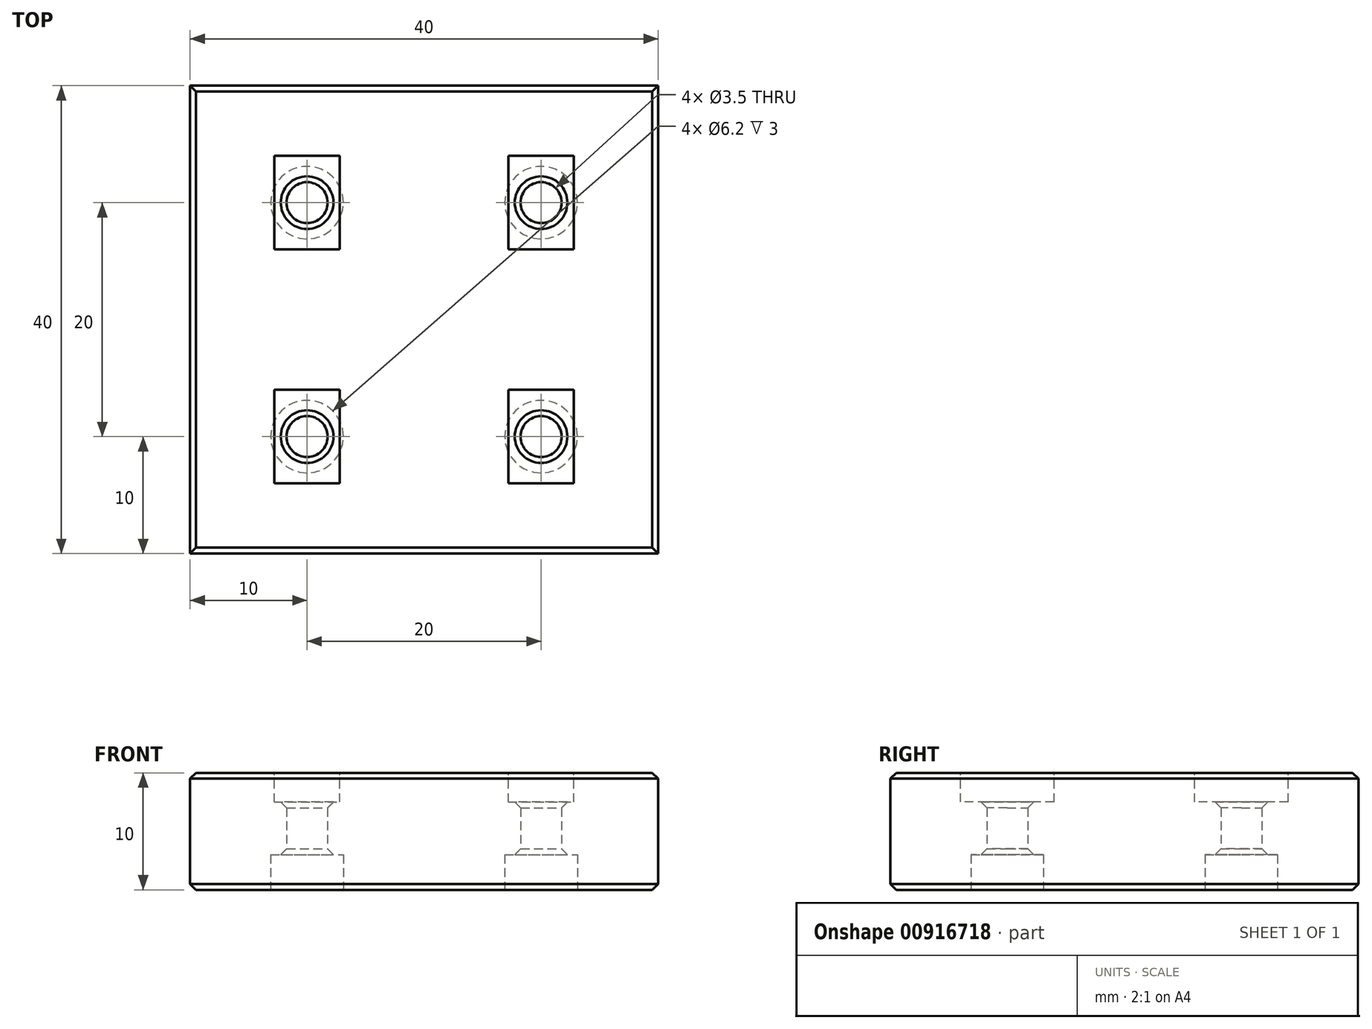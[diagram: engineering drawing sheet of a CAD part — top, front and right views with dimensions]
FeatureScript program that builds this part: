
annotation { "Feature Type Name" : "Feature", "Feature Type Description" : "" }
export const myFeature = defineFeature(function(context is Context, id is Id, definition is map)
    precondition{}
    {
        {
            var Q0;
            Q0=qCreatedBy(makeId("Top.planeOp"),FACE);
            var sketch = newSketch(context, id + "F0", { "sketchPlane" : qUnion([Q0])});
            skLineSegment(sketch, "E0.bottom", {"start": v(-20, 20) * mm, "end": v(20, 20) * mm});
            skLineSegment(sketch, "E0.top", {"start": v(-20, -20) * mm, "end": v(20, -20) * mm});
            skLineSegment(sketch, "E0.left", {"start": v(-20, 20) * mm, "end": v(-20, -20) * mm});
            skLineSegment(sketch, "E0.right", {"start": v(20, 20) * mm, "end": v(20, -20) * mm});
            skCircle(sketch, "E1", {"center": v(-10, 10) * mm, "radius": 1.75 * mm});
            skCircle(sketch, "E2", {"center": v(10, 10) * mm, "radius": 1.75 * mm});
            skCircle(sketch, "E3", {"center": v(10, -10) * mm, "radius": 1.75 * mm});
            skCircle(sketch, "E4", {"center": v(-10, -10) * mm, "radius": 1.75 * mm});
            skSolve(sketch);
        }
        {
            var Q0;
            Q0 = qSketchRegion(id + "F0", true);
            extrude(context, id + "F1", {"entities" : qUnion([Q0]), "depth" : 10 * mm, "offsetDistance" : 25 * mm});
        }
        {
            var Q0;
            Q0=makeQuery(id+"F1.opExtrude","CAP_FACE",FACE,{"disambiguationData":[OSD([sQuery(id+"F0.wireOp",EDGE,"E0.bottom"),sQuery(id+"F0.wireOp",EDGE,"E0.top"),sQuery(id+"F0.wireOp",EDGE,"E0.left"),sQuery(id+"F0.wireOp",EDGE,"E0.right"),sQuery(id+"F0.wireOp",EDGE,"E1"),sQuery(id+"F0.wireOp",EDGE,"E2"),sQuery(id+"F0.wireOp",EDGE,"E3"),sQuery(id+"F0.wireOp",EDGE,"E4")])],"isStart":true});
            var sketch = newSketch(context, id + "F2", { "sketchPlane" : qUnion([Q0])});
            skCircle(sketch, "E5", {"center": v(10, 10) * mm, "radius": 3.1 * mm});
            skCircle(sketch, "E6", {"center": v(10, -10) * mm, "radius": 3.1 * mm});
            skCircle(sketch, "E7", {"center": v(-10, -10) * mm, "radius": 3.1 * mm});
            skCircle(sketch, "E8", {"center": v(-10, 10) * mm, "radius": 3.1 * mm});
            skSolve(sketch);
        }
        {
            var Q0;
            Q0 = qSketchRegion(id + "F2", true);
            extrude(context, id + "F3", {"entities" : qUnion([Q0]), "operationType" : NewBodyOperationType.REMOVE, "oppositeDirection" : true, "depth" : 3 * mm, "offsetDistance" : 25 * mm});
        }
        {
            var Q0;
            Q0=makeQuery(id+"F1.opExtrude","CAP_FACE",FACE,{"disambiguationData":[OSD([sQuery(id+"F0.wireOp",EDGE,"E0.bottom"),sQuery(id+"F0.wireOp",EDGE,"E0.top"),sQuery(id+"F0.wireOp",EDGE,"E0.left"),sQuery(id+"F0.wireOp",EDGE,"E0.right"),sQuery(id+"F0.wireOp",EDGE,"E1"),sQuery(id+"F0.wireOp",EDGE,"E2"),sQuery(id+"F0.wireOp",EDGE,"E3"),sQuery(id+"F0.wireOp",EDGE,"E4")])],"isStart":false});
            var sketch = newSketch(context, id + "F4", { "sketchPlane" : qUnion([Q0])});
            skLineSegment(sketch, "E9.bottom", {"start": v(-12.8, 14) * mm, "end": v(-7.2, 14) * mm});
            skLineSegment(sketch, "E9.top", {"start": v(-12.8, 6) * mm, "end": v(-7.2, 6) * mm});
            skLineSegment(sketch, "E9.left", {"start": v(-12.8, 14) * mm, "end": v(-12.8, 6) * mm});
            skLineSegment(sketch, "E9.right", {"start": v(-7.2, 14) * mm, "end": v(-7.2, 6) * mm});
            skLineSegment(sketch, "E10.bottom", {"start": v(7.2, 14) * mm, "end": v(12.8, 14) * mm});
            skLineSegment(sketch, "E10.top", {"start": v(7.2, 6) * mm, "end": v(12.8, 6) * mm});
            skLineSegment(sketch, "E10.left", {"start": v(7.2, 14) * mm, "end": v(7.2, 6) * mm});
            skLineSegment(sketch, "E10.right", {"start": v(12.8, 14) * mm, "end": v(12.8, 6) * mm});
            skLineSegment(sketch, "E11.bottom", {"start": v(7.2, -6) * mm, "end": v(12.8, -6) * mm});
            skLineSegment(sketch, "E11.top", {"start": v(7.2, -14) * mm, "end": v(12.8, -14) * mm});
            skLineSegment(sketch, "E11.left", {"start": v(7.2, -6) * mm, "end": v(7.2, -14) * mm});
            skLineSegment(sketch, "E11.right", {"start": v(12.8, -6) * mm, "end": v(12.8, -14) * mm});
            skLineSegment(sketch, "E12.bottom", {"start": v(-12.8, -6) * mm, "end": v(-7.2, -6) * mm});
            skLineSegment(sketch, "E12.top", {"start": v(-12.8, -14) * mm, "end": v(-7.2, -14) * mm});
            skLineSegment(sketch, "E12.left", {"start": v(-12.8, -6) * mm, "end": v(-12.8, -14) * mm});
            skLineSegment(sketch, "E12.right", {"start": v(-7.2, -6) * mm, "end": v(-7.2, -14) * mm});
            skSolve(sketch);
        }
        {
            var Q0;
            Q0 = qSketchRegion(id + "F4", true);
            extrude(context, id + "F5", {"entities" : qUnion([Q0]), "operationType" : NewBodyOperationType.REMOVE, "oppositeDirection" : true, "depth" : 2.5 * mm, "offsetDistance" : 25 * mm});
        }
        {
            var Q0;
            Q0=makeQuery(id+"F1.opExtrude","CAP_EDGE",EDGE,{"disambiguationData":[OSD([sQuery(id+"F0.wireOp",EDGE,"E0.left")])],"isStart":false});
            var Q1;
            Q1=makeQuery(id+"F1.opExtrude","CAP_EDGE",EDGE,{"disambiguationData":[OSD([sQuery(id+"F0.wireOp",EDGE,"E0.bottom")])],"isStart":false});
            var Q2;
            Q2=makeQuery(id+"F1.opExtrude","CAP_EDGE",EDGE,{"disambiguationData":[OSD([sQuery(id+"F0.wireOp",EDGE,"E0.right")])],"isStart":false});
            var Q3;
            Q3=makeQuery(id+"F1.opExtrude","CAP_EDGE",EDGE,{"disambiguationData":[OSD([sQuery(id+"F0.wireOp",EDGE,"E0.top")])],"isStart":false});
            var Q4;
            Q4=makeQuery(id+"F5.boolean.opBoolean","COPY",EDGE,{"derivedFrom":makeQuery(id+"F5.opExtrude","CAP_EDGE",EDGE,{"disambiguationData":[OSD([sQuery(id+"F4.wireOp",EDGE,"E11.right")])],"isStart":true})});
            var Q5;
            Q5=makeQuery(id+"F5.boolean.opBoolean","COPY",EDGE,{"derivedFrom":makeQuery(id+"F5.opExtrude","CAP_EDGE",EDGE,{"disambiguationData":[OSD([sQuery(id+"F4.wireOp",EDGE,"E11.top")])],"isStart":true})});
            var Q6;
            Q6=makeQuery(id+"F5.boolean.opBoolean","COPY",EDGE,{"derivedFrom":makeQuery(id+"F5.opExtrude","CAP_EDGE",EDGE,{"disambiguationData":[OSD([sQuery(id+"F4.wireOp",EDGE,"E11.left")])],"isStart":true})});
            var Q7;
            Q7=makeQuery(id+"F5.boolean.opBoolean","COPY",EDGE,{"derivedFrom":makeQuery(id+"F5.opExtrude","CAP_EDGE",EDGE,{"disambiguationData":[OSD([sQuery(id+"F4.wireOp",EDGE,"E11.bottom")])],"isStart":true})});
            var Q8;
            Q8=makeQuery(id+"F5.boolean.opBoolean","COPY",EDGE,{"derivedFrom":makeQuery(id+"F5.opExtrude","CAP_EDGE",EDGE,{"disambiguationData":[OSD([sQuery(id+"F4.wireOp",EDGE,"E12.right")])],"isStart":true})});
            var Q9;
            Q9=makeQuery(id+"F5.boolean.opBoolean","COPY",EDGE,{"derivedFrom":makeQuery(id+"F5.opExtrude","CAP_EDGE",EDGE,{"disambiguationData":[OSD([sQuery(id+"F4.wireOp",EDGE,"E12.left")])],"isStart":true})});
            var Q10;
            Q10=makeQuery(id+"F5.boolean.opBoolean","COPY",EDGE,{"derivedFrom":makeQuery(id+"F5.opExtrude","CAP_EDGE",EDGE,{"disambiguationData":[OSD([sQuery(id+"F4.wireOp",EDGE,"E12.bottom")])],"isStart":true})});
            var Q11;
            Q11=makeQuery(id+"F5.boolean.opBoolean","COPY",EDGE,{"derivedFrom":makeQuery(id+"F5.opExtrude","CAP_EDGE",EDGE,{"disambiguationData":[OSD([sQuery(id+"F4.wireOp",EDGE,"E12.top")])],"isStart":true})});
            var Q12;
            Q12=makeQuery(id+"F5.boolean.opBoolean","COPY",EDGE,{"derivedFrom":makeQuery(id+"F5.opExtrude","CAP_EDGE",EDGE,{"disambiguationData":[OSD([sQuery(id+"F4.wireOp",EDGE,"E9.bottom")])],"isStart":true})});
            var Q13;
            Q13=makeQuery(id+"F5.boolean.opBoolean","COPY",EDGE,{"derivedFrom":makeQuery(id+"F5.opExtrude","CAP_EDGE",EDGE,{"disambiguationData":[OSD([sQuery(id+"F4.wireOp",EDGE,"E9.left")])],"isStart":true})});
            var Q14;
            Q14=makeQuery(id+"F5.boolean.opBoolean","COPY",EDGE,{"derivedFrom":makeQuery(id+"F5.opExtrude","CAP_EDGE",EDGE,{"disambiguationData":[OSD([sQuery(id+"F4.wireOp",EDGE,"E9.top")])],"isStart":true})});
            var Q15;
            Q15=makeQuery(id+"F5.boolean.opBoolean","COPY",EDGE,{"derivedFrom":makeQuery(id+"F5.opExtrude","CAP_EDGE",EDGE,{"disambiguationData":[OSD([sQuery(id+"F4.wireOp",EDGE,"E9.right")])],"isStart":true})});
            var Q16;
            Q16=makeQuery(id+"F5.boolean.opBoolean","COPY",EDGE,{"derivedFrom":makeQuery(id+"F5.opExtrude","CAP_EDGE",EDGE,{"disambiguationData":[OSD([sQuery(id+"F4.wireOp",EDGE,"E10.right")])],"isStart":true})});
            var Q17;
            Q17=makeQuery(id+"F5.boolean.opBoolean","COPY",EDGE,{"derivedFrom":makeQuery(id+"F5.opExtrude","CAP_EDGE",EDGE,{"disambiguationData":[OSD([sQuery(id+"F4.wireOp",EDGE,"E10.bottom")])],"isStart":true})});
            var Q18;
            Q18=makeQuery(id+"F5.boolean.opBoolean","COPY",EDGE,{"derivedFrom":makeQuery(id+"F5.opExtrude","CAP_EDGE",EDGE,{"disambiguationData":[OSD([sQuery(id+"F4.wireOp",EDGE,"E10.left")])],"isStart":true})});
            var Q19;
            Q19=makeQuery(id+"F5.boolean.opBoolean","COPY",EDGE,{"derivedFrom":makeQuery(id+"F5.opExtrude","CAP_EDGE",EDGE,{"disambiguationData":[OSD([sQuery(id+"F4.wireOp",EDGE,"E10.top")])],"isStart":true})});
            chamfer(context, id + "F6", {"entities" : qUnion([Q0, Q1, Q2, Q3, Q4, Q5, Q6, Q7, Q8, Q9, Q10, Q11, Q12, Q13, Q14, Q15, Q16, Q17, Q18, Q19]), "width" : .5 * mm, "tangentPropagation" : true});
        }
        {
            var Q0;
            Q0=makeQuery(id+"F3.boolean.opBoolean","COPY",EDGE,{"derivedFrom":makeQuery(id+"F3.opExtrude","CAP_EDGE",EDGE,{"disambiguationData":[OSD([sQuery(id+"F2.wireOp",EDGE,"E5")])],"isStart":true})});
            var Q1;
            Q1=makeQuery(id+"F3.boolean.opBoolean","COPY",EDGE,{"derivedFrom":makeQuery(id+"F3.opExtrude","CAP_EDGE",EDGE,{"disambiguationData":[OSD([sQuery(id+"F2.wireOp",EDGE,"E8")])],"isStart":true})});
            var Q2;
            Q2=makeQuery(id+"F3.boolean.opBoolean","COPY",EDGE,{"derivedFrom":makeQuery(id+"F3.opExtrude","CAP_EDGE",EDGE,{"disambiguationData":[OSD([sQuery(id+"F2.wireOp",EDGE,"E6")])],"isStart":true})});
            var Q3;
            Q3=makeQuery(id+"F3.boolean.opBoolean","COPY",EDGE,{"derivedFrom":makeQuery(id+"F3.opExtrude","CAP_EDGE",EDGE,{"disambiguationData":[OSD([sQuery(id+"F2.wireOp",EDGE,"E7")])],"isStart":true})});
            var Q4;
            Q4=makeQuery(id+"F3.boolean.opBoolean","INTERSECT",EDGE,{"derivedFrom":[makeQuery(id+"F1.opExtrude","SWEPT_FACE",FACE,{"disambiguationData":[OSD([sQuery(id+"F0.wireOp",EDGE,"E3")])]}),makeQuery(id+"F3.opExtrude","CAP_FACE",FACE,{"disambiguationData":[OSD([sQuery(id+"F2.wireOp",EDGE,"E5")])],"isStart":false})]});
            var Q5;
            Q5=makeQuery(id+"F3.boolean.opBoolean","INTERSECT",EDGE,{"derivedFrom":[makeQuery(id+"F1.opExtrude","SWEPT_FACE",FACE,{"disambiguationData":[OSD([sQuery(id+"F0.wireOp",EDGE,"E4")])]}),makeQuery(id+"F3.opExtrude","CAP_FACE",FACE,{"disambiguationData":[OSD([sQuery(id+"F2.wireOp",EDGE,"E8")])],"isStart":false})]});
            var Q6;
            Q6=makeQuery(id+"F3.boolean.opBoolean","INTERSECT",EDGE,{"derivedFrom":[makeQuery(id+"F1.opExtrude","SWEPT_FACE",FACE,{"disambiguationData":[OSD([sQuery(id+"F0.wireOp",EDGE,"E2")])]}),makeQuery(id+"F3.opExtrude","CAP_FACE",FACE,{"disambiguationData":[OSD([sQuery(id+"F2.wireOp",EDGE,"E6")])],"isStart":false})]});
            var Q7;
            Q7=makeQuery(id+"F3.boolean.opBoolean","INTERSECT",EDGE,{"derivedFrom":[makeQuery(id+"F1.opExtrude","SWEPT_FACE",FACE,{"disambiguationData":[OSD([sQuery(id+"F0.wireOp",EDGE,"E1")])]}),makeQuery(id+"F3.opExtrude","CAP_FACE",FACE,{"disambiguationData":[OSD([sQuery(id+"F2.wireOp",EDGE,"E7")])],"isStart":false})]});
            var Q8;
            Q8=makeQuery(id+"F1.opExtrude","CAP_EDGE",EDGE,{"disambiguationData":[OSD([sQuery(id+"F0.wireOp",EDGE,"E0.left")])],"isStart":true});
            var Q9;
            Q9=makeQuery(id+"F1.opExtrude","CAP_EDGE",EDGE,{"disambiguationData":[OSD([sQuery(id+"F0.wireOp",EDGE,"E0.bottom")])],"isStart":true});
            var Q10;
            Q10=makeQuery(id+"F1.opExtrude","CAP_EDGE",EDGE,{"disambiguationData":[OSD([sQuery(id+"F0.wireOp",EDGE,"E0.top")])],"isStart":true});
            var Q11;
            Q11=makeQuery(id+"F1.opExtrude","CAP_EDGE",EDGE,{"disambiguationData":[OSD([sQuery(id+"F0.wireOp",EDGE,"E0.right")])],"isStart":true});
            var Q12;
            Q12=makeQuery(id+"F5.boolean.opBoolean","INTERSECT",EDGE,{"derivedFrom":[makeQuery(id+"F1.opExtrude","SWEPT_FACE",FACE,{"disambiguationData":[OSD([sQuery(id+"F0.wireOp",EDGE,"E2")])]}),makeQuery(id+"F5.opExtrude","CAP_FACE",FACE,{"disambiguationData":[OSD([sQuery(id+"F4.wireOp",EDGE,"E10.bottom"),sQuery(id+"F4.wireOp",EDGE,"E10.top"),sQuery(id+"F4.wireOp",EDGE,"E10.left"),sQuery(id+"F4.wireOp",EDGE,"E10.right")])],"isStart":false})]});
            var Q13;
            Q13=makeQuery(id+"F5.boolean.opBoolean","INTERSECT",EDGE,{"derivedFrom":[makeQuery(id+"F1.opExtrude","SWEPT_FACE",FACE,{"disambiguationData":[OSD([sQuery(id+"F0.wireOp",EDGE,"E3")])]}),makeQuery(id+"F5.opExtrude","CAP_FACE",FACE,{"disambiguationData":[OSD([sQuery(id+"F4.wireOp",EDGE,"E11.bottom"),sQuery(id+"F4.wireOp",EDGE,"E11.top"),sQuery(id+"F4.wireOp",EDGE,"E11.left"),sQuery(id+"F4.wireOp",EDGE,"E11.right")])],"isStart":false})]});
            var Q14;
            Q14=makeQuery(id+"F5.boolean.opBoolean","INTERSECT",EDGE,{"derivedFrom":[makeQuery(id+"F1.opExtrude","SWEPT_FACE",FACE,{"disambiguationData":[OSD([sQuery(id+"F0.wireOp",EDGE,"E1")])]}),makeQuery(id+"F5.opExtrude","CAP_FACE",FACE,{"disambiguationData":[OSD([sQuery(id+"F4.wireOp",EDGE,"E9.bottom"),sQuery(id+"F4.wireOp",EDGE,"E9.top"),sQuery(id+"F4.wireOp",EDGE,"E9.left"),sQuery(id+"F4.wireOp",EDGE,"E9.right")])],"isStart":false})]});
            var Q15;
            Q15=makeQuery(id+"F5.boolean.opBoolean","INTERSECT",EDGE,{"derivedFrom":[makeQuery(id+"F1.opExtrude","SWEPT_FACE",FACE,{"disambiguationData":[OSD([sQuery(id+"F0.wireOp",EDGE,"E4")])]}),makeQuery(id+"F5.opExtrude","CAP_FACE",FACE,{"disambiguationData":[OSD([sQuery(id+"F4.wireOp",EDGE,"E12.bottom"),sQuery(id+"F4.wireOp",EDGE,"E12.top"),sQuery(id+"F4.wireOp",EDGE,"E12.left"),sQuery(id+"F4.wireOp",EDGE,"E12.right")])],"isStart":false})]});
            chamfer(context, id + "F7", {"entities" : qUnion([Q0, Q1, Q2, Q3, Q4, Q5, Q6, Q7, Q8, Q9, Q10, Q11, Q12, Q13, Q14, Q15]), "width" : 0.5 * mm, "tangentPropagation" : true});
        }
    });
